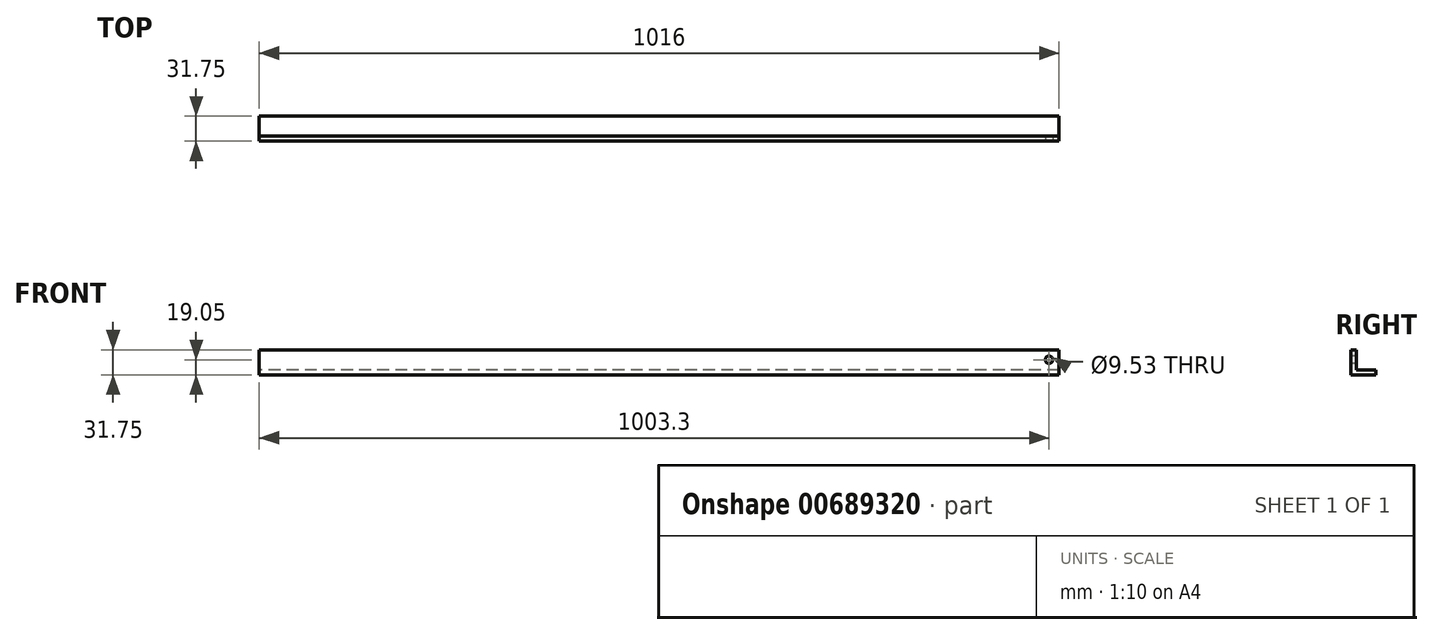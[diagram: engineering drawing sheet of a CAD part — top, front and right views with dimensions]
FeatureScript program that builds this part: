
annotation { "Feature Type Name" : "Feature", "Feature Type Description" : "" }
export const myFeature = defineFeature(function(context is Context, id is Id, definition is map)
    precondition{}
    {
        {
            var Q0;
            Q0=qCreatedBy(makeId("Right.planeOp"),FACE);
            var sketch = newSketch(context, id + "F0", { "sketchPlane" : qUnion([Q0])});
            skLineSegment(sketch, "E0", {"start": v(0, 0) * mm, "end": v(31.75, 0) * mm});
            skLineSegment(sketch, "E1", {"start": v(31.75, 0) * mm, "end": v(31.75, 6.35) * mm});
            skLineSegment(sketch, "E2", {"start": v(31.75, 6.35) * mm, "end": v(6.35, 6.35) * mm});
            skLineSegment(sketch, "E3", {"start": v(6.35, 6.35) * mm, "end": v(6.35, 31.75) * mm});
            skLineSegment(sketch, "E4", {"start": v(6.35, 31.75) * mm, "end": v(0, 31.75) * mm});
            skLineSegment(sketch, "E5", {"start": v(0, 31.75) * mm, "end": v(0, 0) * mm});
            skSolve(sketch);
        }
        {
            var Q0;
            Q0=makeQuery(id+"F0.imprint","IMPRINT",FACE,{"disambiguationData":[TD([[makeQuery(id+"F0.imprint","IMPRINT",EDGE,{"derivedFrom":sQuery(id+"F0.wireOp",EDGE,"E0")}),1.0]])]});
            extrude(context, id + "F1", {"entities" : qUnion([Q0]), "depth" : 1016 * mm, "offsetDistance" : 25.4 * mm});
        }
        {
            var Q0;
            Q0=makeQuery(id+"F1.opExtrude","SWEPT_FACE",FACE,{"disambiguationData":[OSD([sQuery(id+"F0.wireOp",EDGE,"E5")])]});
            var sketch = newSketch(context, id + "F2", { "sketchPlane" : qUnion([Q0])});
            skPoint(sketch, "E6.centerSnap0", {"position": v(1016, 15.88) * mm});
            skCircle(sketch, "E7", {"center": v(1003.3, 19.05) * mm, "radius": 4.76 * mm});
            skSolve(sketch);
        }
        {
            var Q0;
            Q0=makeQuery(id+"F2.imprint","IMPRINT",FACE,{"disambiguationData":[TD([[makeQuery(id+"F2.imprint","IMPRINT",EDGE,{"derivedFrom":sQuery(id+"F2.wireOp",EDGE,"E7")}),1.0]])]});
            extrude(context, id + "F3", {"entities" : qUnion([Q0]), "operationType" : NewBodyOperationType.REMOVE, "endBound" : BoundingType.THROUGH_ALL, "oppositeDirection" : true, "depth" : 25.4 * mm, "offsetDistance" : 25.4 * mm});
        }
    });
